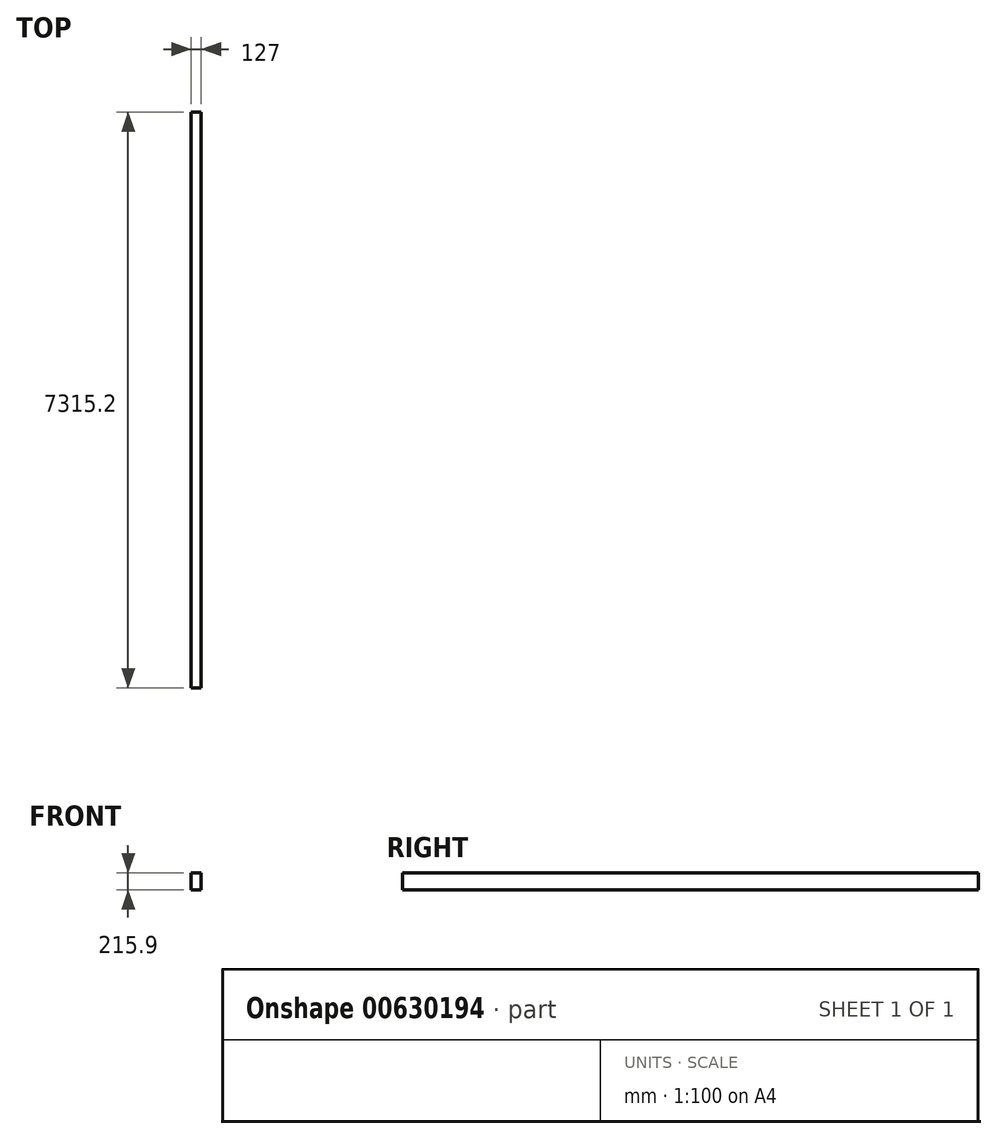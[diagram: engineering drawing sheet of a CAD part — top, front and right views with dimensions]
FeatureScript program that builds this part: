
annotation { "Feature Type Name" : "Feature", "Feature Type Description" : "" }
export const myFeature = defineFeature(function(context is Context, id is Id, definition is map)
    precondition{}
    {
        {
            var Q0;
            Q0=qCreatedBy(makeId("Front.planeOp"),FACE);
            var sketch = newSketch(context, id + "F0", { "sketchPlane" : qUnion([Q0])});
            skLineSegment(sketch, "E0.bottom", {"start": v(0, 0) * mm, "end": v(-127, 0) * mm});
            skLineSegment(sketch, "E0.top", {"start": v(0, 215.9) * mm, "end": v(-127, 215.9) * mm});
            skLineSegment(sketch, "E0.left", {"start": v(0, 0) * mm, "end": v(0, 215.9) * mm});
            skLineSegment(sketch, "E0.right", {"start": v(-127, 0) * mm, "end": v(-127, 215.9) * mm});
            skSolve(sketch);
        }
        {
            var Q0;
            Q0 = qSketchRegion(id + "F0", true);
            extrude(context, id + "F1", {"entities" : qUnion([Q0]), "depth" : 7315.2 * mm, "offsetDistance" : 25.4 * mm});
        }
    });
